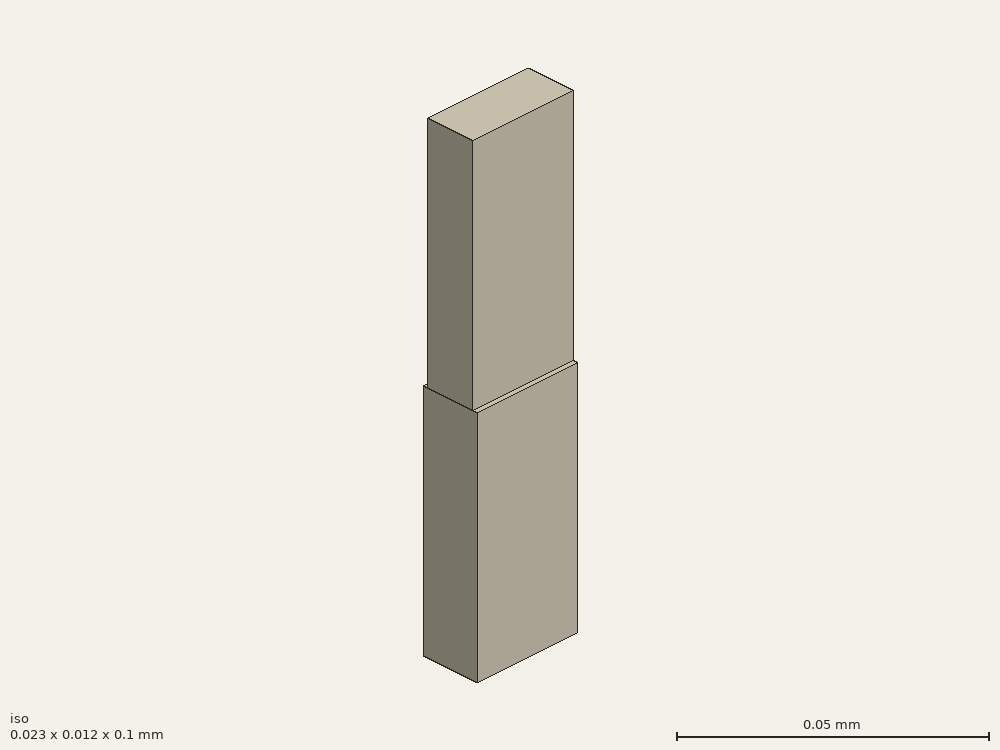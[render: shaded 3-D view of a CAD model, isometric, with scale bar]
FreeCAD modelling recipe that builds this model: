
FCSTD DOCUMENT  (FreeCAD 0.21R33694 (Git))
Label: shorted
License: All rights reserved
LicenseURL: http://en.wikipedia.org/wiki/All_rights_reserved
objects: Part::Part2DObjectPython×4, Part::Extrusion×2, App::FeaturePython×2, Part::FeaturePython×2
note: 8 computed .brp shape members not serialized (recipe doc carries the construction recipe); baked Part::Feature solids carry a one-line shape summary decoded from their .brp

FEATURE [Part::Part2DObjectPython] Rectangle  # Draft 2D object (typed FeaturePython)
  Area = 232.258
  ChamferSize = 0
  Columns = 1
  FilletRadius = 0
  Height = 10.16
  Length = 22.86
  MakeFace = true
  Placement = pos=(-11.43,-5.08,0) rot=(0,0,1;0rad)
  Rows = 1
FEATURE [Part::Extrusion] Extrude
  Base = -> Rectangle
  Dir = (0,0,1)
  DirMode = 2
  FaceMakerClass = Part::FaceMakerBullseye
  LengthFwd = 50
  LengthRev = 0
  Solid = false
  Symmetric = false
FEATURE [Part::Part2DObjectPython] Rectangle001  label="_Pport1"  # Draft 2D object (typed FeaturePython)
  Area = 0.000232258
  ChamferSize = 0
  Columns = 1
  FilletRadius = 0
  Height = 0.01016
  Length = 0.02286
  MakeFace = true
  Placement = pos=(-0.01143,-0.00508,0.05) rot=(0,0,1;0rad)
  Rows = 1
FEATURE [Part::Part2DObjectPython] Line  label="_Pv1"  # Draft 2D object (typed FeaturePython)
  Area = 0
  ChamferSize = 0
  Closed = false
  End = (-1.8e-15,0.00508,0.05)
  FilletRadius = 0
  Length = 0.01016
  MakeFace = true
  Placement = pos=(-0.011,-0.005,3e-15) rot=(0,0,1;0rad)
  Points = (2) [(0.011,-8e-05,0.05),(0.011,0.01008,0.05)]
  Start = (0,-0.00508,0.05)
  Subdivisions = 0
FEATURE [App::FeaturePython] Text  label="_S1(PV){port1}"  # WARN: FeaturePython — macro-defined, semantics opaque (R4)
  Placement = pos=(0.0413747,-0.017509,0) rot=(0,0,1;0rad)
  Text = .
FEATURE [App::FeaturePython] Text002  label="_L1(1,voltage){v1}"  # WARN: FeaturePython — macro-defined, semantics opaque (R4)
  Placement = pos=(0.0413747,-0.017509,0) rot=(0,0,1;0rad)
  Text = .
FEATURE [Part::Part2DObjectPython] Rectangle002  # Draft 2D object (typed FeaturePython)
  Area = 277.978
  ChamferSize = 0
  Columns = 1
  FilletRadius = 0
  Height = 22.86
  Length = 12.16
  MakeFace = true
  Placement = pos=(-11.43,-6.08,0) rot=(0.707107,0.707107,0;3.14159rad)
  Rows = 1
FEATURE [Part::Extrusion] Extrude001  label="Extrude002"
  Base = -> Rectangle002
  Dir = (1e-16,-1e-16,-1)
  DirMode = 2
  FaceMakerClass = Part::FaceMakerBullseye
  LengthFwd = 50
  LengthRev = 0
  Solid = false
  Symmetric = false
FEATURE [Part::FeaturePython] BooleanFragments  # WARN: FeaturePython — macro-defined, semantics opaque (R4)
  Mode = 0
  Objects = -> [Extrude001,Extrude]
  Tolerance = 0
FEATURE [Part::FeaturePython] Clone  label="scaled"  # Draft clone (typed FeaturePython)
  AttacherType = Attacher::AttachEngine3D
  Fuse = false
  Objects = -> [BooleanFragments]
  Scale = (0.001,0.001,0.001)
